# Revit family: Building-IEC309Connections-GEWISS-66IB-INTERLOCKED-SOCKET-OUTLETS-HD_IP66_WITHOUT_BOTTOM_MOD
name_source: partatom
category: Apparecchi elettrici
revit_build: Autodesk Revit 2016 (Build: 20161004_0715(x64)
units: mm (PartAtom-declared; Revit-internal decimal feet)

## family parameters
Condiviso = No
Host = Muro
Mantenere orientamento annotazione = Sì
Numero OmniClass = 23.80.50.14
Punto di calcolo locali = No
Quota connettore circolare = Usa diametro
Sempre verticale = Sì
Taglio con vuoti quando caricato = No
Tipo di parte = Normale
Titolo OmniClass = Plug Connectors

## types (1)
- Building-IEC309Connections-GEWISS-66IB-INTERLOCKED-SOCKET-OUTLETS-HD_IP66_WITHOUT_BOTTOM_MOD
    Altezza da terra = 1128 mm
    Carico apparente = 0 VA
    Catalogue = BUILDING
    Catalogue Range = 66 IB
    Classificazione carico = Altro
    Colour = Red
    Colour: = Red
    Descrizione = I.SOCKET IP66 N.B.3P+E 32A 380V 3H M.D
    EAN code = 8011564066885
    Electrocod = 2222
    Frequency = 50/60 Hz
    Glow Wire Test = 850 °C
    Glow wire test: = 850 °C
    IDF = b704cc15-e102-4c45-bcfd-51753296ccfc
    IDT = b1e88bf2-d9e0-4d22-9355-672d9a796eac
    IP degree = IP66
    Immagine tipo = GW66830.jpg
    Impact resistance at -20 °C = 20J
    Modello = GW66846
    No. of poles = 3P+E
    Number of poles = 3P+E
    Numero poli = 3
    Operating temperature: = -25 +40 °C
    Potenza = 400 V
    Presa = GEWISS - rosso
    Produttore = GEWISS S.p.A.
    Protection = Suitable for modular apps. (6M)
    Rated current (A) = 32
    Rated current (In) = 32
    Rated frequency (Hz) = 50/60 Hz
    Rated voltage = 380-440V
    Reference h = 3
    SEO = Socket outlet
    Shock resistance = > IK10
    Struttura = GEWISS - Grigio RAL - 7035
    Struttura alta = GEWISS - blue
    Technical sheet = https://www.gewiss.com
    Thermo-pressure with ball = 80
    Type of use = Heavy duty
    Typology = Vertical
    URL = https://www.gewiss.com
    Version file RFA = 18.0
    Vetro = Vetro
    With back-mounting box = No
    Working temperature = -25 ÷ +40 °C

note: source unit labels omitted for Thermo-pressure with ball — the stored unit's dimension contradicts the parameter name (converter mislabeling)
